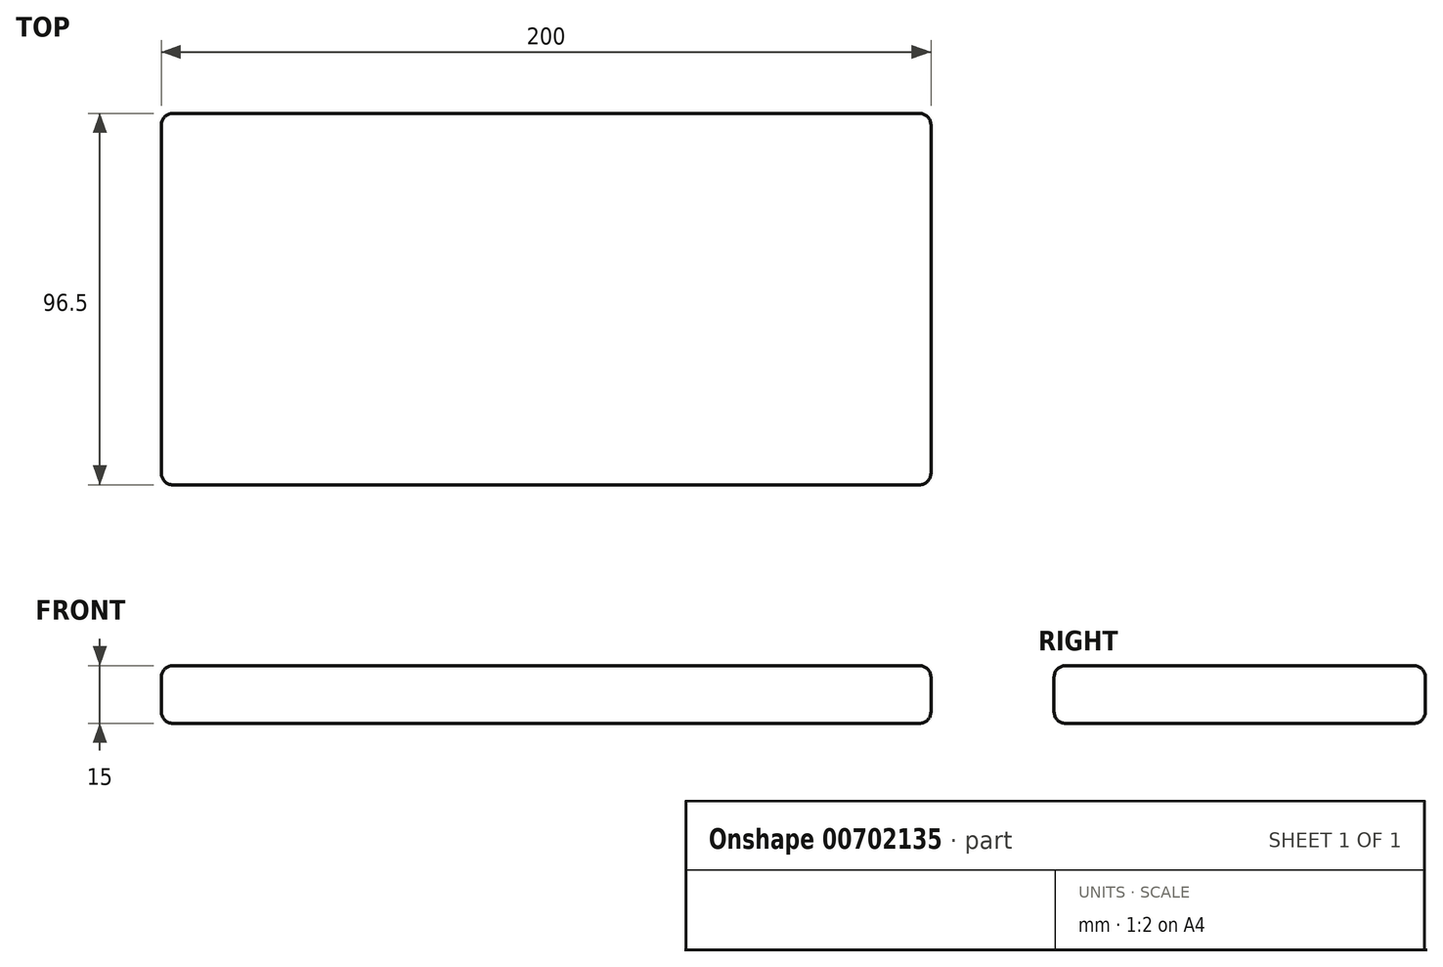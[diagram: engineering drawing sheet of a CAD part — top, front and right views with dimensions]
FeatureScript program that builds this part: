
annotation { "Feature Type Name" : "Feature", "Feature Type Description" : "" }
export const myFeature = defineFeature(function(context is Context, id is Id, definition is map)
    precondition{}
    {
        {
            var Q0;
            Q0=qCreatedBy(makeId("Top.planeOp"),FACE);
            var sketch = newSketch(context, id + "F0", { "sketchPlane" : qUnion([Q0])});
            skLineSegment(sketch, "E0.bottom", {"start": v(100, 48.25) * mm, "end": v(-100, 48.25) * mm});
            skLineSegment(sketch, "E0.top", {"start": v(100, -48.25) * mm, "end": v(-100, -48.25) * mm});
            skLineSegment(sketch, "E0.left", {"start": v(100, 48.25) * mm, "end": v(100, -48.25) * mm});
            skLineSegment(sketch, "E0.right", {"start": v(-100, 48.25) * mm, "end": v(-100, -48.25) * mm});
            skPoint(sketch, "E0.middle", {"position": v(0, 0) * mm});
            skSolve(sketch);
        }
        {
            var Q0;
            Q0=makeQuery(id+"F0.imprint","IMPRINT",FACE,{"disambiguationData":[TD([[makeQuery(id+"F0.imprint","IMPRINT",EDGE,{"derivedFrom":sQuery(id+"F0.wireOp",EDGE,"E0.bottom")}),1.0]])]});
            extrude(context, id + "F1", {"entities" : qUnion([Q0]), "depth" : 15 * mm, "offsetDistance" : 25 * mm});
        }
        {
            var Q0;
            Q0=makeQuery(id+"F1.opExtrude","CAP_EDGE",EDGE,{"disambiguationData":[OSD([sQuery(id+"F0.wireOp",EDGE,"E0.bottom")])],"isStart":true});
            var Q1;
            Q1=makeQuery(id+"F1.opExtrude","CAP_EDGE",EDGE,{"disambiguationData":[OSD([sQuery(id+"F0.wireOp",EDGE,"E0.bottom")])],"isStart":false});
            var Q2;
            Q2=makeQuery(id+"F1.opExtrude","SWEPT_EDGE",EDGE,{"disambiguationData":[OSD([sQuery(id+"F0.wireOp",EDGE,"E0.bottom"),sQuery(id+"F0.wireOp",EDGE,"E0.right")])]});
            var Q3;
            Q3=makeQuery(id+"F1.opExtrude","CAP_EDGE",EDGE,{"disambiguationData":[OSD([sQuery(id+"F0.wireOp",EDGE,"E0.right")])],"isStart":true});
            var Q4;
            Q4=makeQuery(id+"F1.opExtrude","CAP_EDGE",EDGE,{"disambiguationData":[OSD([sQuery(id+"F0.wireOp",EDGE,"E0.right")])],"isStart":false});
            var Q5;
            Q5=makeQuery(id+"F1.opExtrude","SWEPT_EDGE",EDGE,{"disambiguationData":[OSD([sQuery(id+"F0.wireOp",EDGE,"E0.top"),sQuery(id+"F0.wireOp",EDGE,"E0.right")])]});
            var Q6;
            Q6=makeQuery(id+"F1.opExtrude","CAP_EDGE",EDGE,{"disambiguationData":[OSD([sQuery(id+"F0.wireOp",EDGE,"E0.top")])],"isStart":true});
            var Q7;
            Q7=makeQuery(id+"F1.opExtrude","CAP_EDGE",EDGE,{"disambiguationData":[OSD([sQuery(id+"F0.wireOp",EDGE,"E0.top")])],"isStart":false});
            var Q8;
            Q8=makeQuery(id+"F1.opExtrude","CAP_EDGE",EDGE,{"disambiguationData":[OSD([sQuery(id+"F0.wireOp",EDGE,"E0.left")])],"isStart":true});
            var Q9;
            Q9=makeQuery(id+"F1.opExtrude","SWEPT_EDGE",EDGE,{"disambiguationData":[OSD([sQuery(id+"F0.wireOp",EDGE,"E0.top"),sQuery(id+"F0.wireOp",EDGE,"E0.left")])]});
            var Q10;
            Q10=makeQuery(id+"F1.opExtrude","CAP_EDGE",EDGE,{"disambiguationData":[OSD([sQuery(id+"F0.wireOp",EDGE,"E0.left")])],"isStart":false});
            var Q11;
            Q11=makeQuery(id+"F1.opExtrude","SWEPT_EDGE",EDGE,{"disambiguationData":[OSD([sQuery(id+"F0.wireOp",EDGE,"E0.bottom"),sQuery(id+"F0.wireOp",EDGE,"E0.left")])]});
            fillet(context, id + "F2", {"entities" : qUnion([Q0, Q1, Q2, Q3, Q4, Q5, Q6, Q7, Q8, Q9, Q10, Q11]), "radius" : 3 * mm, "tangentPropagation" : true, "allowEdgeOverflow" : false});
        }
    });
